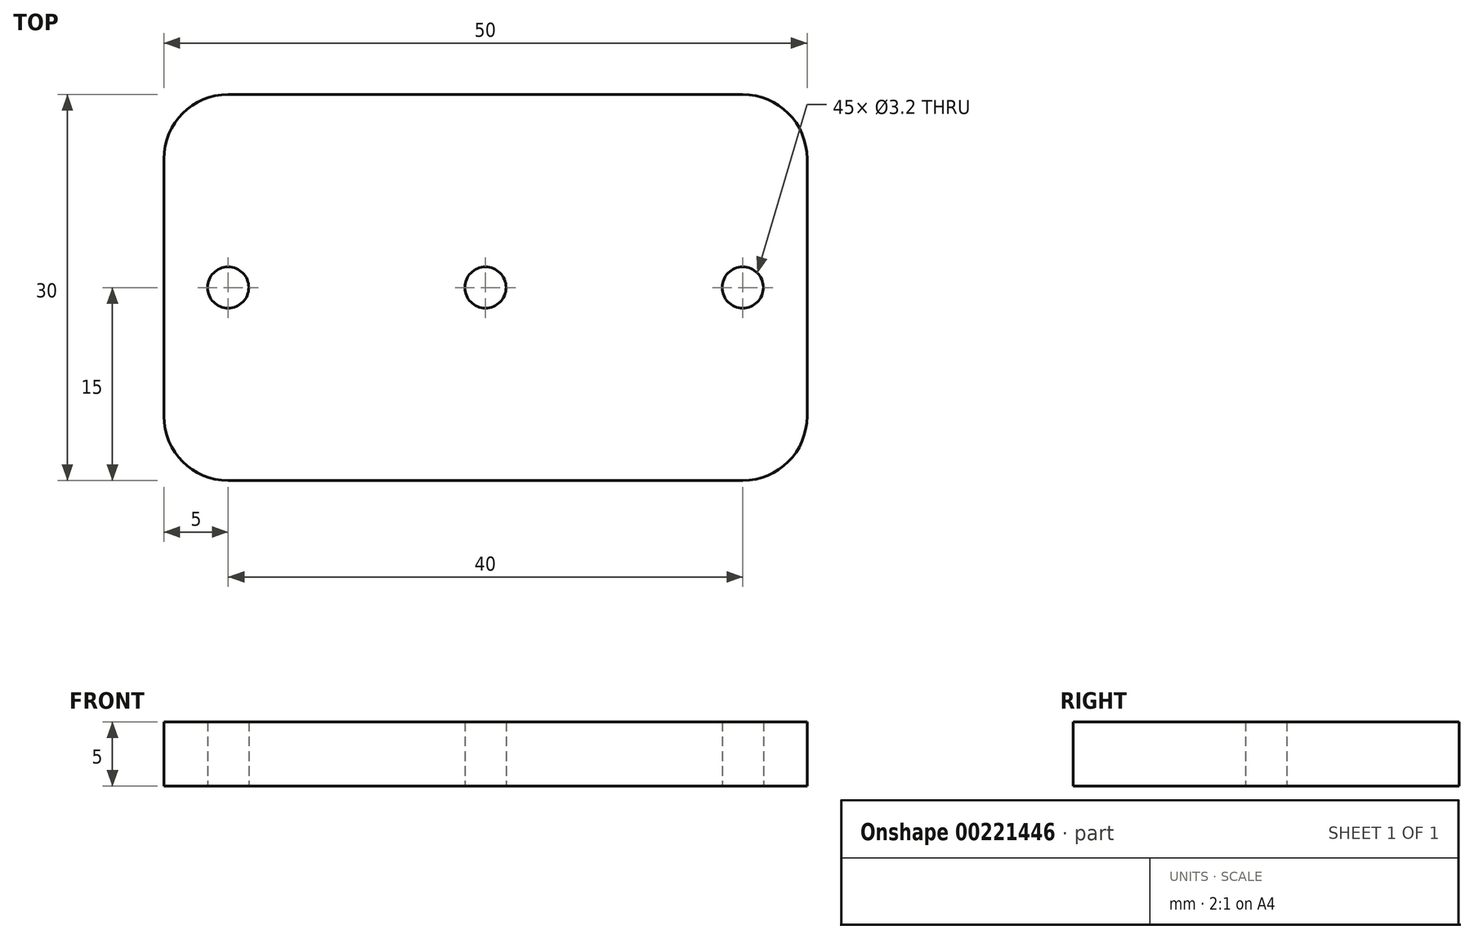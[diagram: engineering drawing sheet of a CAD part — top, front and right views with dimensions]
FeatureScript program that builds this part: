
annotation { "Feature Type Name" : "Feature", "Feature Type Description" : "" }
export const myFeature = defineFeature(function(context is Context, id is Id, definition is map)
    precondition{}
    {
        {
            var Q0;
            Q0=qCreatedBy(makeId("Top.planeOp"),FACE);
            var sketch = newSketch(context, id + "F0", { "sketchPlane" : qUnion([Q0])});
            skLineSegment(sketch, "E0.bottom", {"start": v(20, 15) * mm, "end": v(-20, 15) * mm});
            skLineSegment(sketch, "E0.top", {"start": v(20, -15) * mm, "end": v(-20, -15) * mm});
            skLineSegment(sketch, "E0.left", {"start": v(25, 10) * mm, "end": v(25, -10) * mm});
            skLineSegment(sketch, "E0.right", {"start": v(-25, 10) * mm, "end": v(-25, -10) * mm});
            skPoint(sketch, "E0.middle", {"position": v(0, 0) * mm});
            skLineSegment(sketch, "E1", {"start": v(-10, 15) * mm, "end": v(-10, -15) * mm, "construction": true});
            skLineSegment(sketch, "E2", {"start": v(10, 15) * mm, "end": v(10, -15) * mm, "construction": true});
            skLineSegment(sketch, "E3", {"start": v(-15, 15) * mm, "end": v(-15, -15) * mm, "construction": true});
            skCircle(sketch, "E4", {"center": v(-20, 0) * mm, "radius": 1.6 * mm});
            skLineSegment(sketch, "E5", {"start": v(0, 15) * mm, "end": v(0, -15) * mm, "construction": true});
            skCircle(sketch, "E6.MirrorC", {"center": v(20, 0) * mm, "radius": 1.6 * mm});
            skCircle(sketch, "E7", {"center": v(0, 0) * mm, "radius": 1.6 * mm});
            skPoint(sketch, "E8.visualSharp", {"position": v(-25, 15) * mm});
            skArc(sketch, "E8.filletArc", {"start": v(-20, 15) * mm, "mid": v(-23.54, 13.54) * mm, "end": v(-25, 10) * mm});
            skPoint(sketch, "E9.visualSharp", {"position": v(25, 15) * mm});
            skArc(sketch, "E9.filletArc", {"start": v(25, 10) * mm, "mid": v(23.54, 13.54) * mm, "end": v(20, 15) * mm});
            skPoint(sketch, "E10.visualSharp", {"position": v(25, -15) * mm});
            skArc(sketch, "E10.filletArc", {"start": v(20, -15) * mm, "mid": v(23.54, -13.54) * mm, "end": v(25, -10) * mm});
            skPoint(sketch, "E11.visualSharp", {"position": v(-25, -15) * mm});
            skArc(sketch, "E11.filletArc", {"start": v(-25, -10) * mm, "mid": v(-23.54, -13.54) * mm, "end": v(-20, -15) * mm});
            skSolve(sketch);
        }
        {
            var Q0;
            Q0 = qSketchRegion(id + "F0", true);
            extrude(context, id + "F1", {"entities" : qUnion([Q0]), "depth" : 5 * mm});
        }
    });
